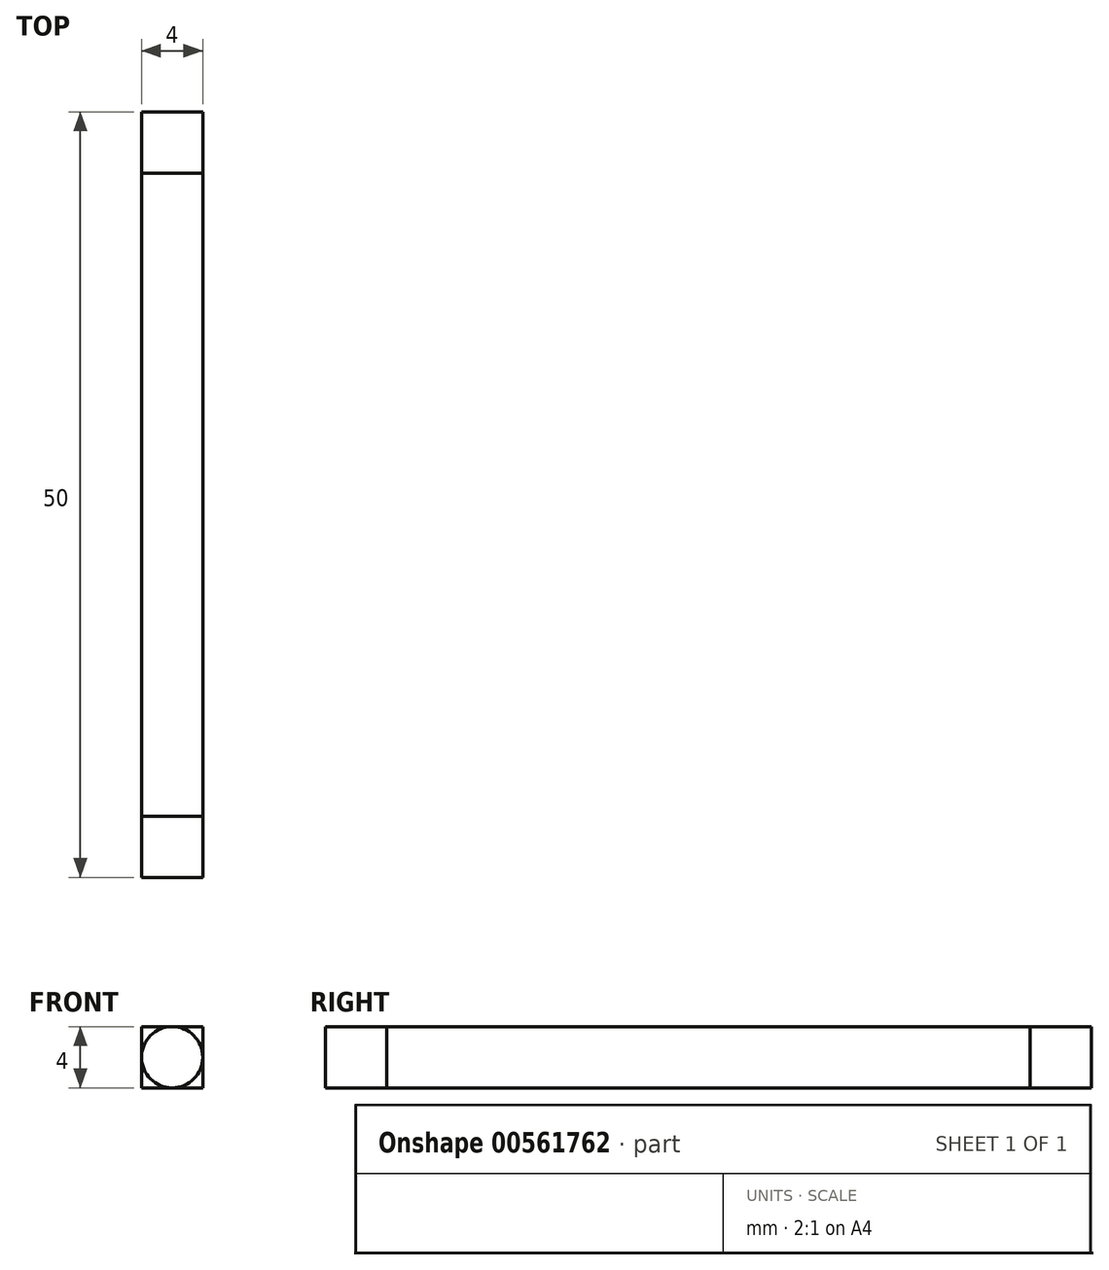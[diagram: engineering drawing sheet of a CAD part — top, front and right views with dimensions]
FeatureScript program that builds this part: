
annotation { "Feature Type Name" : "Feature", "Feature Type Description" : "" }
export const myFeature = defineFeature(function(context is Context, id is Id, definition is map)
    precondition{}
    {
        {
            var Q0;
            Q0=qCreatedBy(makeId("Front.planeOp"),FACE);
            var sketch = newSketch(context, id + "F0", { "sketchPlane" : qUnion([Q0])});
            skLineSegment(sketch, "E0.bottom", {"start": v(2, 2) * mm, "end": v(-2, 2) * mm});
            skLineSegment(sketch, "E0.top", {"start": v(2, -2) * mm, "end": v(-2, -2) * mm});
            skLineSegment(sketch, "E0.left", {"start": v(2, 2) * mm, "end": v(2, -2) * mm});
            skLineSegment(sketch, "E0.right", {"start": v(-2, 2) * mm, "end": v(-2, -2) * mm});
            skPoint(sketch, "E0.middle", {"position": v(0, 0) * mm});
            skSolve(sketch);
        }
        {
            var Q0;
            Q0 = qSketchRegion(id + "F0", true);
            extrude(context, id + "F1", {"entities" : qUnion([Q0]), "depth" : 50 * mm, "offsetDistance" : 25 * mm});
        }
        {
            var Q0;
            Q0=makeQuery(id+"F1.opExtrude","CAP_FACE",FACE,{"disambiguationData":[OSD([sQuery(id+"F0.wireOp",EDGE,"E0.bottom"),sQuery(id+"F0.wireOp",EDGE,"E0.top"),sQuery(id+"F0.wireOp",EDGE,"E0.left"),sQuery(id+"F0.wireOp",EDGE,"E0.right")])],"isStart":true});
            var sketch = newSketch(context, id + "F2", { "sketchPlane" : qUnion([Q0])});
            skCircle(sketch, "E1", {"center": v(0, 0) * mm, "radius": 2 * mm});
            skLineSegment(sketch, "E2", {"start": v(-2, 2) * mm, "end": v(-2, -2) * mm});
            skLineSegment(sketch, "E3", {"start": v(-2, -2) * mm, "end": v(2, -2) * mm});
            skLineSegment(sketch, "E4", {"start": v(2, -2) * mm, "end": v(2, 2) * mm});
            skLineSegment(sketch, "E5", {"start": v(2, 2) * mm, "end": v(-2, 2) * mm});
            skSolve(sketch);
        }
        {
            var Q0;
            {var subQ0=sQuery(id+"F2.wireOp",EDGE,"E5");var subQ1=sQuery(id+"F2.wireOp",EDGE,"E1");var subQ2=makeQuery(id+"F2.imprint","INTERSECT",VERTEX,{"derivedFrom":[subQ1,subQ0]});Q0=makeQuery(id+"F2.imprint","IMPRINT",FACE,{"disambiguationData":[TD([[makeQuery(id+"F2.imprint","IMPRINT",EDGE,{"disambiguationData":[TD([[subQ2,-1.0]])],"derivedFrom":subQ1}),-1.0]])]});}
            var Q1;
            {var subQ0=sQuery(id+"F2.wireOp",EDGE,"E2");var subQ1=sQuery(id+"F2.wireOp",EDGE,"E1");var subQ2=makeQuery(id+"F2.imprint","INTERSECT",VERTEX,{"derivedFrom":[subQ1,subQ0]});Q1=makeQuery(id+"F2.imprint","IMPRINT",FACE,{"disambiguationData":[TD([[makeQuery(id+"F2.imprint","IMPRINT",EDGE,{"disambiguationData":[TD([[subQ2,-1.0]])],"derivedFrom":subQ1}),-1.0]])]});}
            var Q2;
            {var subQ0=sQuery(id+"F2.wireOp",EDGE,"E4");var subQ1=sQuery(id+"F2.wireOp",EDGE,"E1");var subQ2=makeQuery(id+"F2.imprint","INTERSECT",VERTEX,{"derivedFrom":[subQ1,subQ0]});Q2=makeQuery(id+"F2.imprint","IMPRINT",FACE,{"disambiguationData":[TD([[makeQuery(id+"F2.imprint","IMPRINT",EDGE,{"disambiguationData":[TD([[subQ2,1.0]])],"derivedFrom":subQ1}),-1.0]])]});}
            var Q3;
            {var subQ0=sQuery(id+"F2.wireOp",EDGE,"E5");var subQ1=sQuery(id+"F2.wireOp",EDGE,"E1");var subQ2=makeQuery(id+"F2.imprint","INTERSECT",VERTEX,{"derivedFrom":[subQ1,subQ0]});Q3=makeQuery(id+"F2.imprint","IMPRINT",FACE,{"disambiguationData":[TD([[makeQuery(id+"F2.imprint","IMPRINT",EDGE,{"disambiguationData":[TD([[subQ2,1.0]])],"derivedFrom":subQ1}),-1.0]])]});}
            extrude(context, id + "F3", {"entities" : qUnion([Q0, Q1, Q2, Q3]), "operationType" : NewBodyOperationType.REMOVE, "oppositeDirection" : true, "depth" : 4 * mm, "offsetDistance" : 25 * mm});
        }
        {
            var Q0;
            Q0=makeQuery(id+"F1.opExtrude","CAP_FACE",FACE,{"disambiguationData":[OSD([sQuery(id+"F0.wireOp",EDGE,"E0.bottom"),sQuery(id+"F0.wireOp",EDGE,"E0.top"),sQuery(id+"F0.wireOp",EDGE,"E0.left"),sQuery(id+"F0.wireOp",EDGE,"E0.right")])],"isStart":false});
            var sketch = newSketch(context, id + "F4", { "sketchPlane" : qUnion([Q0])});
            skCircle(sketch, "E6", {"center": v(0, 0) * mm, "radius": 2 * mm});
            skLineSegment(sketch, "E7", {"start": v(-2, 2) * mm, "end": v(-2, -2) * mm});
            skLineSegment(sketch, "E8", {"start": v(-2, -2) * mm, "end": v(2, -2) * mm});
            skLineSegment(sketch, "E9", {"start": v(2, -2) * mm, "end": v(2, 2) * mm});
            skLineSegment(sketch, "E10", {"start": v(2, 2) * mm, "end": v(-2, 2) * mm});
            skSolve(sketch);
        }
        {
            var Q0;
            {var subQ0=sQuery(id+"F4.wireOp",EDGE,"E10");var subQ1=sQuery(id+"F4.wireOp",EDGE,"E6");var subQ2=makeQuery(id+"F4.imprint","INTERSECT",VERTEX,{"derivedFrom":[subQ1,subQ0]});Q0=makeQuery(id+"F4.imprint","IMPRINT",FACE,{"disambiguationData":[TD([[makeQuery(id+"F4.imprint","IMPRINT",EDGE,{"disambiguationData":[TD([[subQ2,-1.0]])],"derivedFrom":subQ1}),-1.0]])]});}
            var Q1;
            {var subQ0=sQuery(id+"F4.wireOp",EDGE,"E7");var subQ1=sQuery(id+"F4.wireOp",EDGE,"E6");var subQ2=makeQuery(id+"F4.imprint","INTERSECT",VERTEX,{"derivedFrom":[subQ1,subQ0]});Q1=makeQuery(id+"F4.imprint","IMPRINT",FACE,{"disambiguationData":[TD([[makeQuery(id+"F4.imprint","IMPRINT",EDGE,{"disambiguationData":[TD([[subQ2,-1.0]])],"derivedFrom":subQ1}),-1.0]])]});}
            var Q2;
            {var subQ0=sQuery(id+"F4.wireOp",EDGE,"E9");var subQ1=sQuery(id+"F4.wireOp",EDGE,"E6");var subQ2=makeQuery(id+"F4.imprint","INTERSECT",VERTEX,{"derivedFrom":[subQ1,subQ0]});Q2=makeQuery(id+"F4.imprint","IMPRINT",FACE,{"disambiguationData":[TD([[makeQuery(id+"F4.imprint","IMPRINT",EDGE,{"disambiguationData":[TD([[subQ2,1.0]])],"derivedFrom":subQ1}),-1.0]])]});}
            var Q3;
            {var subQ0=sQuery(id+"F4.wireOp",EDGE,"E10");var subQ1=sQuery(id+"F4.wireOp",EDGE,"E6");var subQ2=makeQuery(id+"F4.imprint","INTERSECT",VERTEX,{"derivedFrom":[subQ1,subQ0]});Q3=makeQuery(id+"F4.imprint","IMPRINT",FACE,{"disambiguationData":[TD([[makeQuery(id+"F4.imprint","IMPRINT",EDGE,{"disambiguationData":[TD([[subQ2,1.0]])],"derivedFrom":subQ1}),-1.0]])]});}
            extrude(context, id + "F5", {"entities" : qUnion([Q0, Q1, Q2, Q3]), "operationType" : NewBodyOperationType.REMOVE, "oppositeDirection" : true, "depth" : 4 * mm, "offsetDistance" : 25 * mm});
        }
    });
